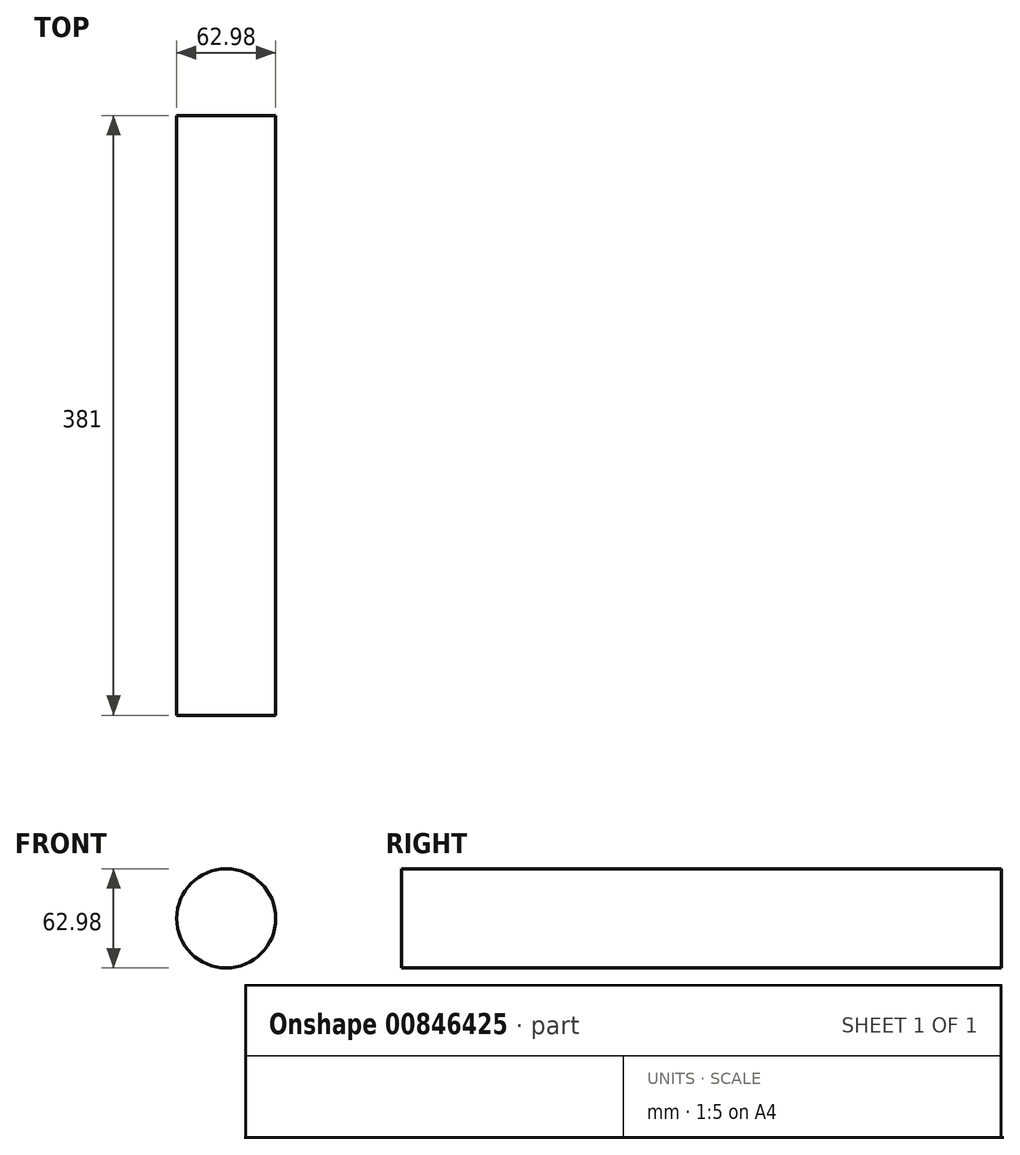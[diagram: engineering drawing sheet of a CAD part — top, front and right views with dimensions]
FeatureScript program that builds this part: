
annotation { "Feature Type Name" : "Feature", "Feature Type Description" : "" }
export const myFeature = defineFeature(function(context is Context, id is Id, definition is map)
    precondition{}
    {
        {
            var Q0;
            Q0=qCreatedBy(makeId("Front.planeOp"),FACE);
            var sketch = newSketch(context, id + "F0", { "sketchPlane" : qUnion([Q0])});
            skCircle(sketch, "E0", {"center": v(0, 0) * mm, "radius": 31.5 * mm});
            skSolve(sketch);
        }
        {
            var Q0;
            Q0 = qSketchRegion(id + "F0", true);
            extrude(context, id + "F1", {"entities" : qUnion([Q0]), "depth" : 381 * mm, "offsetDistance" : 25.4 * mm});
        }
    });
